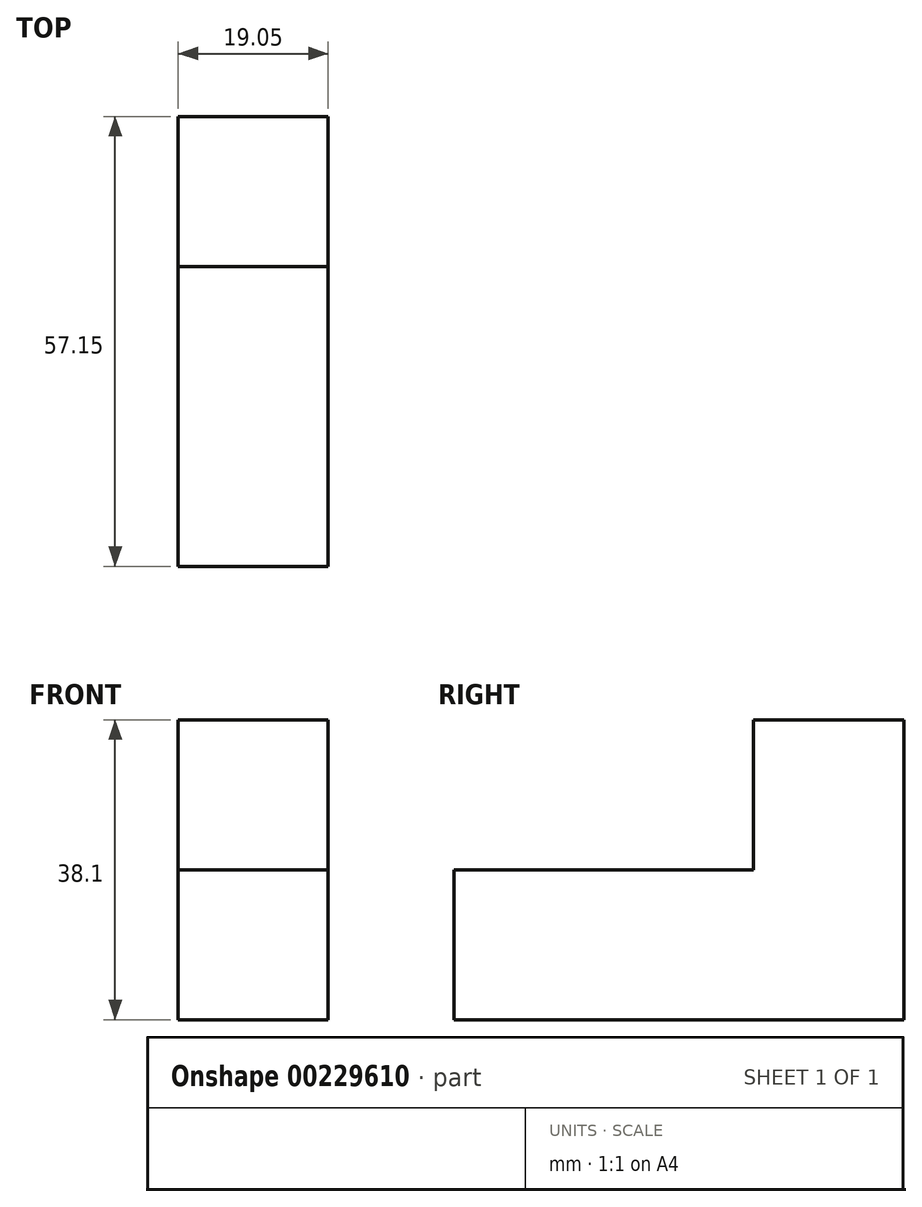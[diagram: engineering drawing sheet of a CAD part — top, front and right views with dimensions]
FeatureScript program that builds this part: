
annotation { "Feature Type Name" : "Feature", "Feature Type Description" : "" }
export const myFeature = defineFeature(function(context is Context, id is Id, definition is map)
    precondition{}
    {
        {
            var Q0;
            Q0=qCreatedBy(makeId("Top.planeOp"),FACE);
            var sketch = newSketch(context, id + "F0", { "sketchPlane" : qUnion([Q0])});
            skLineSegment(sketch, "E0.bottom", {"start": v(-50.12, -30.82) * mm, "end": v(-31.07, -30.82) * mm});
            skLineSegment(sketch, "E0.top", {"start": v(-50.12, 26.33) * mm, "end": v(-31.07, 26.33) * mm});
            skLineSegment(sketch, "E0.left", {"start": v(-50.12, -30.82) * mm, "end": v(-50.12, 26.33) * mm});
            skLineSegment(sketch, "E0.right", {"start": v(-31.07, -30.82) * mm, "end": v(-31.07, 26.33) * mm});
            skSolve(sketch);
        }
        {
            var Q0;
            Q0 = qSketchRegion(id + "F0", true);
            extrude(context, id + "F1", {"entities" : qUnion([Q0]), "depth" : 19.05 * mm});
        }
        {
            var Q0;
            Q0=makeQuery(id+"F1.opExtrude","CAP_FACE",FACE,{"disambiguationData":[OSD([sQuery(id+"F0.wireOp",EDGE,"E0.bottom"),sQuery(id+"F0.wireOp",EDGE,"E0.top"),sQuery(id+"F0.wireOp",EDGE,"E0.left"),sQuery(id+"F0.wireOp",EDGE,"E0.right")])],"isStart":false});
            var sketch = newSketch(context, id + "F2", { "sketchPlane" : qUnion([Q0])});
            skLineSegment(sketch, "E1.bottom", {"start": v(-31.07, 26.33) * mm, "end": v(-50.12, 26.33) * mm});
            skLineSegment(sketch, "E1.top", {"start": v(-31.07, 7.22) * mm, "end": v(-50.12, 7.22) * mm});
            skLineSegment(sketch, "E1.left", {"start": v(-31.07, 26.33) * mm, "end": v(-31.07, 7.22) * mm});
            skLineSegment(sketch, "E1.right", {"start": v(-50.12, 26.33) * mm, "end": v(-50.12, 7.22) * mm});
            skSolve(sketch);
        }
        {
            var Q0;
            Q0=makeQuery(id+"F2.imprint","IMPRINT",FACE,{"disambiguationData":[TD([[makeQuery(id+"F2.imprint","IMPRINT",EDGE,{"derivedFrom":sQuery(id+"F2.wireOp",EDGE,"E1.bottom")}),-1.0]])]});
            extrude(context, id + "F3", {"entities" : qUnion([Q0]), "operationType" : NewBodyOperationType.ADD, "depth" : 19.05 * mm});
        }
    });
